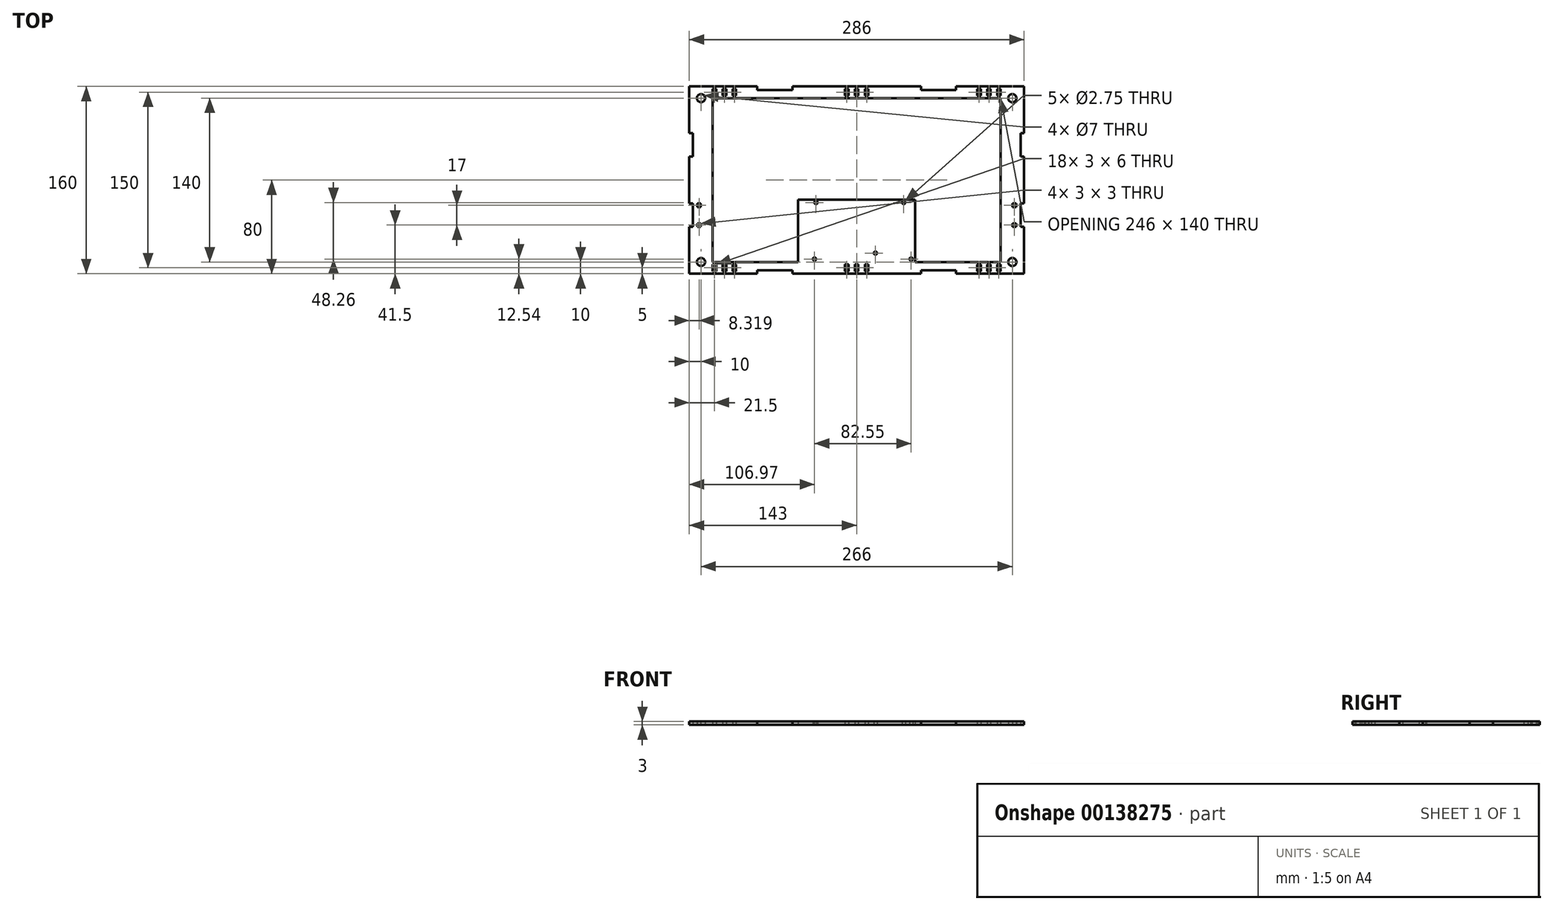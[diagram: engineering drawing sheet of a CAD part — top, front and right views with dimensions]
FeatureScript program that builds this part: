
annotation { "Feature Type Name" : "Feature", "Feature Type Description" : "" }
export const myFeature = defineFeature(function(context is Context, id is Id, definition is map)
    precondition{}
    {
        {
            var Q0;
            Q0=qCreatedBy(makeId("Top.planeOp"),FACE);
            var sketch = newSketch(context, id + "F0", { "sketchPlane" : qUnion([Q0])});
            skLineSegment(sketch, "E0.bottom", {"start": v(-143, 80) * mm, "end": v(-85, 80) * mm});
            skLineSegment(sketch, "E0.top", {"start": v(-143, -80) * mm, "end": v(-85, -80) * mm});
            skLineSegment(sketch, "E0.left", {"start": v(-143, 80) * mm, "end": v(-143, 40) * mm});
            skLineSegment(sketch, "E0.right", {"start": v(143, 80) * mm, "end": v(143, 40) * mm});
            skPoint(sketch, "E0.middle", {"position": v(0, 0) * mm});
            skLineSegment(sketch, "E1", {"start": v(-143, -80) * mm, "end": v(-133, -80) * mm, "construction": true});
            skLineSegment(sketch, "E2", {"start": v(-133, -80) * mm, "end": v(-133, -70) * mm, "construction": true});
            skCircle(sketch, "E3", {"center": v(-133, -70) * mm, "radius": 3.5 * mm});
            skCircle(sketch, "E4.MirrorC", {"center": v(133, -70) * mm, "radius": 3.5 * mm});
            skCircle(sketch, "E5.MirrorC", {"center": v(133, 70) * mm, "radius": 3.5 * mm});
            skCircle(sketch, "E6.MirrorC", {"center": v(-133, 70) * mm, "radius": 3.5 * mm});
            skLineSegment(sketch, "E7.bottom", {"start": v(123, 70) * mm, "end": v(-123, 70) * mm});
            skLineSegment(sketch, "E7.top", {"start": v(123, -70) * mm, "end": v(50, -70) * mm});
            skLineSegment(sketch, "E7.left", {"start": v(123, 70) * mm, "end": v(123, -70) * mm});
            skLineSegment(sketch, "E7.right", {"start": v(-123, 70) * mm, "end": v(-123, -70) * mm});
            skLineSegment(sketch, "E8", {"start": v(0, -70) * mm, "end": v(0, -15) * mm, "construction": true});
            skLineSegment(sketch, "E9", {"start": v(-50, -70) * mm, "end": v(-50, -16.66) * mm, "construction": true});
            skLineSegment(sketch, "E10", {"start": v(-50, -70) * mm, "end": v(-50, -67.46) * mm, "construction": true});
            skLineSegment(sketch, "E11", {"start": v(-36.03, -70) * mm, "end": v(-36.03, -67.46) * mm, "construction": true});
            skCircle(sketch, "E12", {"center": v(-36.03, -67.46) * mm, "radius": 1.38 * mm, "construction": true});
            skCircle(sketch, "E13", {"center": v(-36.03, -67.46) * mm, "radius": 1.38 * mm});
            skLineSegment(sketch, "E14", {"start": v(-50, -70) * mm, "end": v(-50, -19.2) * mm, "construction": true});
            skLineSegment(sketch, "E15", {"start": v(-34.76, -16.66) * mm, "end": v(-34.76, -19.2) * mm, "construction": true});
            skCircle(sketch, "E16", {"center": v(-34.76, -19.2) * mm, "radius": 1.38 * mm});
            skLineSegment(sketch, "E17", {"start": v(50, -70) * mm, "end": v(50, -16.66) * mm});
            skLineSegment(sketch, "E18", {"start": v(50, -16.66) * mm, "end": v(-43, -16.66) * mm});
            skLineSegment(sketch, "E19", {"start": v(-50, -16.66) * mm, "end": v(-50, -70) * mm});
            skLineSegment(sketch, "E20", {"start": v(-43, -16.66) * mm, "end": v(40.17, -16.66) * mm, "construction": true});
            skLineSegment(sketch, "E21", {"start": v(-34.76, -19.2) * mm, "end": v(40.17, -19.2) * mm, "construction": true});
            skCircle(sketch, "E22", {"center": v(40.17, -19.2) * mm, "radius": 1.38 * mm});
            skLineSegment(sketch, "E23", {"start": v(46.52, -70) * mm, "end": v(46.52, -67.46) * mm, "construction": true});
            skCircle(sketch, "E24", {"center": v(46.52, -67.46) * mm, "radius": 1.38 * mm});
            skLineSegment(sketch, "E25", {"start": v(16.04, -63.76) * mm, "end": v(16.04, -62.38) * mm, "construction": true});
            skCircle(sketch, "E26", {"center": v(16.04, -62.38) * mm, "radius": 1.38 * mm, "construction": true});
            skLineSegment(sketch, "E27.bottom", {"start": v(-50, -70) * mm, "end": v(-123, -70) * mm});
            skLineSegment(sketch, "E27.top", {"start": v(-43, -16.66) * mm, "end": v(-50, -16.66) * mm});
            skLineSegment(sketch, "E27.left", {"start": v(-50, -70) * mm, "end": v(-50, -16.66) * mm});
            skPoint(sketch, "E28.visualSharp", {"position": v(-123, -16.66) * mm});
            skCircle(sketch, "E29", {"center": v(16.04, -62.38) * mm, "radius": 1.38 * mm});
            skLineSegment(sketch, "E30", {"start": v(0, -80) * mm, "end": v(-55, -80) * mm, "construction": true});
            skLineSegment(sketch, "E31", {"start": v(-55, -80) * mm, "end": v(-55, -77) * mm});
            skLineSegment(sketch, "E32", {"start": v(-55, -77) * mm, "end": v(-85, -77) * mm});
            skLineSegment(sketch, "E33", {"start": v(-85, -77) * mm, "end": v(-85, -80) * mm});
            skLineSegment(sketch, "E34.trimOffspring", {"start": v(-55, -80) * mm, "end": v(55, -80) * mm});
            skLineSegment(sketch, "E35", {"start": v(0, -80) * mm, "end": v(55, -80) * mm, "construction": true});
            skLineSegment(sketch, "E36", {"start": v(55, -80) * mm, "end": v(55, -77) * mm, "construction": true});
            skLineSegment(sketch, "E37", {"start": v(55, -77) * mm, "end": v(85, -77) * mm, "construction": true});
            skLineSegment(sketch, "E38", {"start": v(55, -80) * mm, "end": v(55, -77) * mm});
            skLineSegment(sketch, "E39", {"start": v(55, -77) * mm, "end": v(85, -77) * mm});
            skLineSegment(sketch, "E40", {"start": v(85, -77) * mm, "end": v(85, -80) * mm});
            skLineSegment(sketch, "E41.trimOffspring", {"start": v(85, -80) * mm, "end": v(143, -80) * mm});
            skPoint(sketch, "E42.start.orphan", {"position": v(143, 0) * mm});
            skLineSegment(sketch, "E43", {"start": v(143, 0) * mm, "end": v(143, -20) * mm, "construction": true});
            skLineSegment(sketch, "E44", {"start": v(143, -20) * mm, "end": v(140, -20) * mm});
            skLineSegment(sketch, "E45", {"start": v(140, -20) * mm, "end": v(140, -40) * mm});
            skLineSegment(sketch, "E46", {"start": v(140, -40) * mm, "end": v(143, -40) * mm});
            skLineSegment(sketch, "E47", {"start": v(143, 0) * mm, "end": v(143, 20) * mm, "construction": true});
            skLineSegment(sketch, "E48", {"start": v(143, 20) * mm, "end": v(140, 20) * mm, "construction": true});
            skLineSegment(sketch, "E49", {"start": v(140, 20) * mm, "end": v(140, 40) * mm, "construction": true});
            skLineSegment(sketch, "E50", {"start": v(143, 20) * mm, "end": v(140, 20) * mm});
            skLineSegment(sketch, "E51", {"start": v(140, 20) * mm, "end": v(140, 40) * mm});
            skLineSegment(sketch, "E52", {"start": v(140, 40) * mm, "end": v(143, 40) * mm});
            skLineSegment(sketch, "E53.trimOffspring", {"start": v(143, 20) * mm, "end": v(143, -20) * mm});
            skLineSegment(sketch, "E54.trimOffspring", {"start": v(143, -40) * mm, "end": v(143, -80) * mm});
            skLineSegment(sketch, "E55", {"start": v(-143, 0) * mm, "end": v(143, 0) * mm, "construction": true});
            skLineSegment(sketch, "E56.MirrorCS", {"start": v(-140, 40) * mm, "end": v(-143, 40) * mm});
            skLineSegment(sketch, "E57.MirrorCS", {"start": v(-140, 20) * mm, "end": v(-140, 40) * mm, "construction": true});
            skLineSegment(sketch, "E58.MirrorCS", {"start": v(-143, 20) * mm, "end": v(-140, 20) * mm, "construction": true});
            skLineSegment(sketch, "E59.MirrorCS", {"start": v(-140, -20) * mm, "end": v(-140, -40) * mm});
            skLineSegment(sketch, "E60.MirrorCS", {"start": v(-143, -20) * mm, "end": v(-140, -20) * mm});
            skLineSegment(sketch, "E61.MirrorCS", {"start": v(-140, -40) * mm, "end": v(-143, -40) * mm});
            skLineSegment(sketch, "E62.MirrorCS", {"start": v(55, 77) * mm, "end": v(85, 77) * mm, "construction": true});
            skLineSegment(sketch, "E63.MirrorCS", {"start": v(85, 77) * mm, "end": v(85, 80) * mm});
            skLineSegment(sketch, "E64.MirrorCS", {"start": v(55, 80) * mm, "end": v(55, 77) * mm, "construction": true});
            skLineSegment(sketch, "E65.MirrorCS", {"start": v(-55, 77) * mm, "end": v(-85, 77) * mm});
            skLineSegment(sketch, "E66.MirrorCS", {"start": v(-85, 77) * mm, "end": v(-85, 80) * mm});
            skLineSegment(sketch, "E67.MirrorCS", {"start": v(-55, 80) * mm, "end": v(-55, 77) * mm});
            skLineSegment(sketch, "E68", {"start": v(-140, 40) * mm, "end": v(-140, 20) * mm});
            skLineSegment(sketch, "E69", {"start": v(-143, 20) * mm, "end": v(-140, 20) * mm});
            skLineSegment(sketch, "E70", {"start": v(55, 80) * mm, "end": v(55, 77) * mm});
            skLineSegment(sketch, "E71", {"start": v(55, 77) * mm, "end": v(85, 77) * mm});
            skLineSegment(sketch, "E72.trimOffspring", {"start": v(-55, 80) * mm, "end": v(55, 80) * mm});
            skLineSegment(sketch, "E73.trimOffspring", {"start": v(85, 80) * mm, "end": v(143, 80) * mm});
            skLineSegment(sketch, "E74.trimOffspring", {"start": v(-143, 20) * mm, "end": v(-143, -20) * mm});
            skLineSegment(sketch, "E75.trimOffspring", {"start": v(-143, -40) * mm, "end": v(-143, -80) * mm});
            skLineSegment(sketch, "E76", {"start": v(-140, -30) * mm, "end": v(-123, -30) * mm, "construction": true});
            skLineSegment(sketch, "E77", {"start": v(-133.18, -10) * mm, "end": v(-133.18, -45.75) * mm, "construction": true});
            skLineSegment(sketch, "E78", {"start": v(-133.18, -30) * mm, "end": v(-133.18, -23) * mm, "construction": true});
            skLineSegment(sketch, "E79.bottom", {"start": v(-133.18, -23) * mm, "end": v(-136.18, -23) * mm});
            skLineSegment(sketch, "E79.top", {"start": v(-133.18, -20) * mm, "end": v(-136.18, -20) * mm});
            skLineSegment(sketch, "E79.left", {"start": v(-133.18, -23) * mm, "end": v(-133.18, -20) * mm});
            skLineSegment(sketch, "E79.right", {"start": v(-136.18, -23) * mm, "end": v(-136.18, -20) * mm});
            skLineSegment(sketch, "E80.MirrorCS", {"start": v(-136.18, -37) * mm, "end": v(-136.18, -40) * mm});
            skLineSegment(sketch, "E81.MirrorCS", {"start": v(-133.18, -37) * mm, "end": v(-133.18, -40) * mm});
            skLineSegment(sketch, "E82.MirrorCS", {"start": v(-133.18, -37) * mm, "end": v(-136.18, -37) * mm});
            skLineSegment(sketch, "E83.MirrorCS", {"start": v(-133.18, -40) * mm, "end": v(-136.18, -40) * mm});
            skLineSegment(sketch, "E84.MirrorCS", {"start": v(133.18, -37) * mm, "end": v(133.18, -40) * mm});
            skLineSegment(sketch, "E85.MirrorCS", {"start": v(136.18, -37) * mm, "end": v(136.18, -40) * mm});
            skLineSegment(sketch, "E86.MirrorCS", {"start": v(136.18, -23) * mm, "end": v(136.18, -20) * mm});
            skLineSegment(sketch, "E87.MirrorCS", {"start": v(133.18, -23) * mm, "end": v(136.18, -23) * mm});
            skLineSegment(sketch, "E88.MirrorCS", {"start": v(133.18, -30) * mm, "end": v(133.18, -23) * mm, "construction": true});
            skLineSegment(sketch, "E89.MirrorCS", {"start": v(133.18, -23) * mm, "end": v(133.18, -20) * mm});
            skLineSegment(sketch, "E90.MirrorCS", {"start": v(133.18, -20) * mm, "end": v(136.18, -20) * mm});
            skLineSegment(sketch, "E91.MirrorCS", {"start": v(133.18, -37) * mm, "end": v(136.18, -37) * mm});
            skLineSegment(sketch, "E92.MirrorCS", {"start": v(133.18, -40) * mm, "end": v(136.18, -40) * mm});
            skLineSegment(sketch, "E93", {"start": v(0, -80) * mm, "end": v(0, -78) * mm, "construction": true});
            skLineSegment(sketch, "E94", {"start": v(0, -78) * mm, "end": v(-1.5, -78) * mm});
            skLineSegment(sketch, "E95", {"start": v(-1.5, -78) * mm, "end": v(-1.5, -75) * mm});
            skLineSegment(sketch, "E96", {"start": v(1.5, -75) * mm, "end": v(1.5, -78) * mm});
            skLineSegment(sketch, "E97", {"start": v(1.5, -78) * mm, "end": v(0, -78) * mm});
            skLineSegment(sketch, "E98", {"start": v(-1.5, -78) * mm, "end": v(-7, -78) * mm, "construction": true});
            skLineSegment(sketch, "E99.bottom", {"start": v(-7, -78) * mm, "end": v(-10, -78) * mm});
            skLineSegment(sketch, "E99.left", {"start": v(-7, -78) * mm, "end": v(-7, -75) * mm});
            skLineSegment(sketch, "E99.right", {"start": v(-10, -78) * mm, "end": v(-10, -75) * mm});
            skLineSegment(sketch, "E100", {"start": v(1.5, -78) * mm, "end": v(7, -78) * mm, "construction": true});
            skLineSegment(sketch, "E101.bottom", {"start": v(7, -78) * mm, "end": v(10, -78) * mm});
            skLineSegment(sketch, "E101.top", {"start": v(7, -72) * mm, "end": v(10, -72) * mm});
            skLineSegment(sketch, "E101.left", {"start": v(7, -78) * mm, "end": v(7, -72) * mm});
            skLineSegment(sketch, "E101.right", {"start": v(10, -78) * mm, "end": v(10, -72) * mm});
            skLineSegment(sketch, "E102", {"start": v(1.5, -75) * mm, "end": v(1.5, -72) * mm});
            skLineSegment(sketch, "E103", {"start": v(1.5, -72) * mm, "end": v(-1.5, -72) * mm});
            skLineSegment(sketch, "E104", {"start": v(-1.5, -72) * mm, "end": v(-1.5, -75) * mm});
            skLineSegment(sketch, "E105", {"start": v(-10, -75) * mm, "end": v(-10, -72) * mm});
            skLineSegment(sketch, "E106", {"start": v(-10, -72) * mm, "end": v(-7, -72) * mm});
            skLineSegment(sketch, "E107", {"start": v(-7, -72) * mm, "end": v(-7, -75) * mm});
            skLineSegment(sketch, "E108", {"start": v(-10, -78) * mm, "end": v(-123, -78) * mm, "construction": true});
            skLineSegment(sketch, "E109.bottom", {"start": v(-123, -78) * mm, "end": v(-120, -78) * mm});
            skLineSegment(sketch, "E109.top", {"start": v(-123, -72) * mm, "end": v(-120, -72) * mm});
            skLineSegment(sketch, "E109.left", {"start": v(-123, -78) * mm, "end": v(-123, -72) * mm});
            skLineSegment(sketch, "E109.right", {"start": v(-120, -78) * mm, "end": v(-120, -72) * mm});
            skLineSegment(sketch, "E110", {"start": v(-120, -78) * mm, "end": v(-114.5, -78) * mm, "construction": true});
            skLineSegment(sketch, "E111.bottom", {"start": v(-114.5, -78) * mm, "end": v(-111.5, -78) * mm});
            skLineSegment(sketch, "E111.top", {"start": v(-114.5, -72) * mm, "end": v(-111.5, -72) * mm});
            skLineSegment(sketch, "E111.left", {"start": v(-114.5, -78) * mm, "end": v(-114.5, -72) * mm});
            skLineSegment(sketch, "E111.right", {"start": v(-111.5, -78) * mm, "end": v(-111.5, -72) * mm});
            skLineSegment(sketch, "E112", {"start": v(-111.5, -78) * mm, "end": v(-106, -78) * mm, "construction": true});
            skLineSegment(sketch, "E113.bottom", {"start": v(-106, -78) * mm, "end": v(-103, -78) * mm});
            skLineSegment(sketch, "E113.top", {"start": v(-106, -72) * mm, "end": v(-103, -72) * mm});
            skLineSegment(sketch, "E113.left", {"start": v(-106, -78) * mm, "end": v(-106, -72) * mm});
            skLineSegment(sketch, "E113.right", {"start": v(-103, -78) * mm, "end": v(-103, -72) * mm});
            skLineSegment(sketch, "E114", {"start": v(0, -70) * mm, "end": v(0, -80) * mm, "construction": true});
            skLineSegment(sketch, "E115.MirrorCS", {"start": v(123, -78) * mm, "end": v(120, -78) * mm});
            skLineSegment(sketch, "E116.MirrorCS", {"start": v(106, -78) * mm, "end": v(103, -78) * mm});
            skLineSegment(sketch, "E117.MirrorCS", {"start": v(123, -72) * mm, "end": v(120, -72) * mm});
            skLineSegment(sketch, "E118.MirrorCS", {"start": v(123, -78) * mm, "end": v(123, -72) * mm});
            skLineSegment(sketch, "E119.MirrorCS", {"start": v(120, -78) * mm, "end": v(120, -72) * mm});
            skLineSegment(sketch, "E120.MirrorCS", {"start": v(120, -78) * mm, "end": v(114.5, -78) * mm, "construction": true});
            skLineSegment(sketch, "E121.MirrorCS", {"start": v(114.5, -72) * mm, "end": v(111.5, -72) * mm});
            skLineSegment(sketch, "E122.MirrorCS", {"start": v(114.5, -78) * mm, "end": v(111.5, -78) * mm});
            skLineSegment(sketch, "E123.MirrorCS", {"start": v(114.5, -78) * mm, "end": v(114.5, -72) * mm});
            skLineSegment(sketch, "E124.MirrorCS", {"start": v(111.5, -78) * mm, "end": v(111.5, -72) * mm});
            skLineSegment(sketch, "E125.MirrorCS", {"start": v(111.5, -78) * mm, "end": v(106, -78) * mm, "construction": true});
            skLineSegment(sketch, "E126.MirrorCS", {"start": v(103, -78) * mm, "end": v(103, -72) * mm});
            skLineSegment(sketch, "E127.MirrorCS", {"start": v(106, -72) * mm, "end": v(103, -72) * mm});
            skLineSegment(sketch, "E128.MirrorCS", {"start": v(106, -78) * mm, "end": v(106, -72) * mm});
            skLineSegment(sketch, "E129.MirrorCS", {"start": v(1.5, 72) * mm, "end": v(-1.5, 72) * mm});
            skLineSegment(sketch, "E130.MirrorCS", {"start": v(-1.5, 78) * mm, "end": v(-1.5, 75) * mm});
            skLineSegment(sketch, "E131.MirrorCS", {"start": v(1.5, 75) * mm, "end": v(1.5, 78) * mm});
            skLineSegment(sketch, "E132.MirrorCS", {"start": v(-1.5, 78) * mm, "end": v(-7, 78) * mm, "construction": true});
            skLineSegment(sketch, "E133.MirrorCS", {"start": v(1.5, 78) * mm, "end": v(0, 78) * mm});
            skLineSegment(sketch, "E134.MirrorCS", {"start": v(-7, 78) * mm, "end": v(-7, 75) * mm});
            skLineSegment(sketch, "E135.MirrorCS", {"start": v(-1.5, 72) * mm, "end": v(-1.5, 75) * mm});
            skLineSegment(sketch, "E136.MirrorCS", {"start": v(7, 78) * mm, "end": v(7, 72) * mm});
            skLineSegment(sketch, "E137.MirrorCS", {"start": v(1.5, 75) * mm, "end": v(1.5, 72) * mm});
            skLineSegment(sketch, "E138.MirrorCS", {"start": v(1.5, 78) * mm, "end": v(7, 78) * mm, "construction": true});
            skLineSegment(sketch, "E139.MirrorCS", {"start": v(-10, 75) * mm, "end": v(-10, 72) * mm});
            skLineSegment(sketch, "E140.MirrorCS", {"start": v(0, 78) * mm, "end": v(-1.5, 78) * mm});
            skLineSegment(sketch, "E141.MirrorCS", {"start": v(-10, 72) * mm, "end": v(-7, 72) * mm});
            skLineSegment(sketch, "E142.MirrorCS", {"start": v(-7, 72) * mm, "end": v(-7, 75) * mm});
            skLineSegment(sketch, "E143.MirrorCS", {"start": v(-7, 78) * mm, "end": v(-10, 78) * mm});
            skLineSegment(sketch, "E144.MirrorCS", {"start": v(7, 72) * mm, "end": v(10, 72) * mm});
            skLineSegment(sketch, "E145.MirrorCS", {"start": v(-10, 78) * mm, "end": v(-10, 75) * mm});
            skLineSegment(sketch, "E146.MirrorCS", {"start": v(10, 78) * mm, "end": v(10, 72) * mm});
            skLineSegment(sketch, "E147.MirrorCS", {"start": v(7, 78) * mm, "end": v(10, 78) * mm});
            skLineSegment(sketch, "E148.MirrorCS", {"start": v(-123, 72) * mm, "end": v(-120, 72) * mm});
            skLineSegment(sketch, "E149.MirrorCS", {"start": v(-123, 78) * mm, "end": v(-120, 78) * mm});
            skLineSegment(sketch, "E150.MirrorCS", {"start": v(-123, 78) * mm, "end": v(-123, 72) * mm});
            skLineSegment(sketch, "E151.MirrorCS", {"start": v(-103, 78) * mm, "end": v(-103, 72) * mm});
            skLineSegment(sketch, "E152.MirrorCS", {"start": v(-106, 78) * mm, "end": v(-106, 72) * mm});
            skLineSegment(sketch, "E153.MirrorCS", {"start": v(-106, 72) * mm, "end": v(-103, 72) * mm});
            skLineSegment(sketch, "E154.MirrorCS", {"start": v(-106, 78) * mm, "end": v(-103, 78) * mm});
            skLineSegment(sketch, "E155.MirrorCS", {"start": v(-111.5, 78) * mm, "end": v(-106, 78) * mm, "construction": true});
            skLineSegment(sketch, "E156.MirrorCS", {"start": v(-111.5, 78) * mm, "end": v(-111.5, 72) * mm});
            skLineSegment(sketch, "E157.MirrorCS", {"start": v(-114.5, 78) * mm, "end": v(-114.5, 72) * mm});
            skLineSegment(sketch, "E158.MirrorCS", {"start": v(-120, 78) * mm, "end": v(-114.5, 78) * mm, "construction": true});
            skLineSegment(sketch, "E159.MirrorCS", {"start": v(-120, 78) * mm, "end": v(-120, 72) * mm});
            skLineSegment(sketch, "E160.MirrorCS", {"start": v(-114.5, 72) * mm, "end": v(-111.5, 72) * mm});
            skLineSegment(sketch, "E161.MirrorCS", {"start": v(-114.5, 78) * mm, "end": v(-111.5, 78) * mm});
            skLineSegment(sketch, "E162.MirrorCS", {"start": v(106, 78) * mm, "end": v(106, 72) * mm});
            skLineSegment(sketch, "E163.MirrorCS", {"start": v(106, 72) * mm, "end": v(103, 72) * mm});
            skLineSegment(sketch, "E164.MirrorCS", {"start": v(106, 78) * mm, "end": v(103, 78) * mm});
            skLineSegment(sketch, "E165.MirrorCS", {"start": v(114.5, 78) * mm, "end": v(114.5, 72) * mm});
            skLineSegment(sketch, "E166.MirrorCS", {"start": v(123, 78) * mm, "end": v(120, 78) * mm});
            skLineSegment(sketch, "E167.MirrorCS", {"start": v(123, 72) * mm, "end": v(120, 72) * mm});
            skLineSegment(sketch, "E168.MirrorCS", {"start": v(114.5, 78) * mm, "end": v(111.5, 78) * mm});
            skLineSegment(sketch, "E169.MirrorCS", {"start": v(111.5, 78) * mm, "end": v(106, 78) * mm, "construction": true});
            skLineSegment(sketch, "E170.MirrorCS", {"start": v(123, 78) * mm, "end": v(123, 72) * mm});
            skLineSegment(sketch, "E171.MirrorCS", {"start": v(120, 78) * mm, "end": v(120, 72) * mm});
            skLineSegment(sketch, "E172.MirrorCS", {"start": v(111.5, 78) * mm, "end": v(111.5, 72) * mm});
            skLineSegment(sketch, "E173.MirrorCS", {"start": v(103, 78) * mm, "end": v(103, 72) * mm});
            skLineSegment(sketch, "E174.MirrorCS", {"start": v(120, 78) * mm, "end": v(114.5, 78) * mm, "construction": true});
            skLineSegment(sketch, "E175.MirrorCS", {"start": v(114.5, 72) * mm, "end": v(111.5, 72) * mm});
            skSolve(sketch);
        }
        {
            var Q0;
            Q0=makeQuery(id+"F0.imprint","IMPRINT",FACE,{"disambiguationData":[TD([[makeQuery(id+"F0.imprint","IMPRINT",EDGE,{"derivedFrom":sQuery(id+"F0.wireOp",EDGE,"E0.bottom")}),-1.0]])]});
            extrude(context, id + "F1", {"entities" : qUnion([Q0]), "endBound" : BoundingType.SYMMETRIC, "depth" : 3 * mm});
        }
    });
